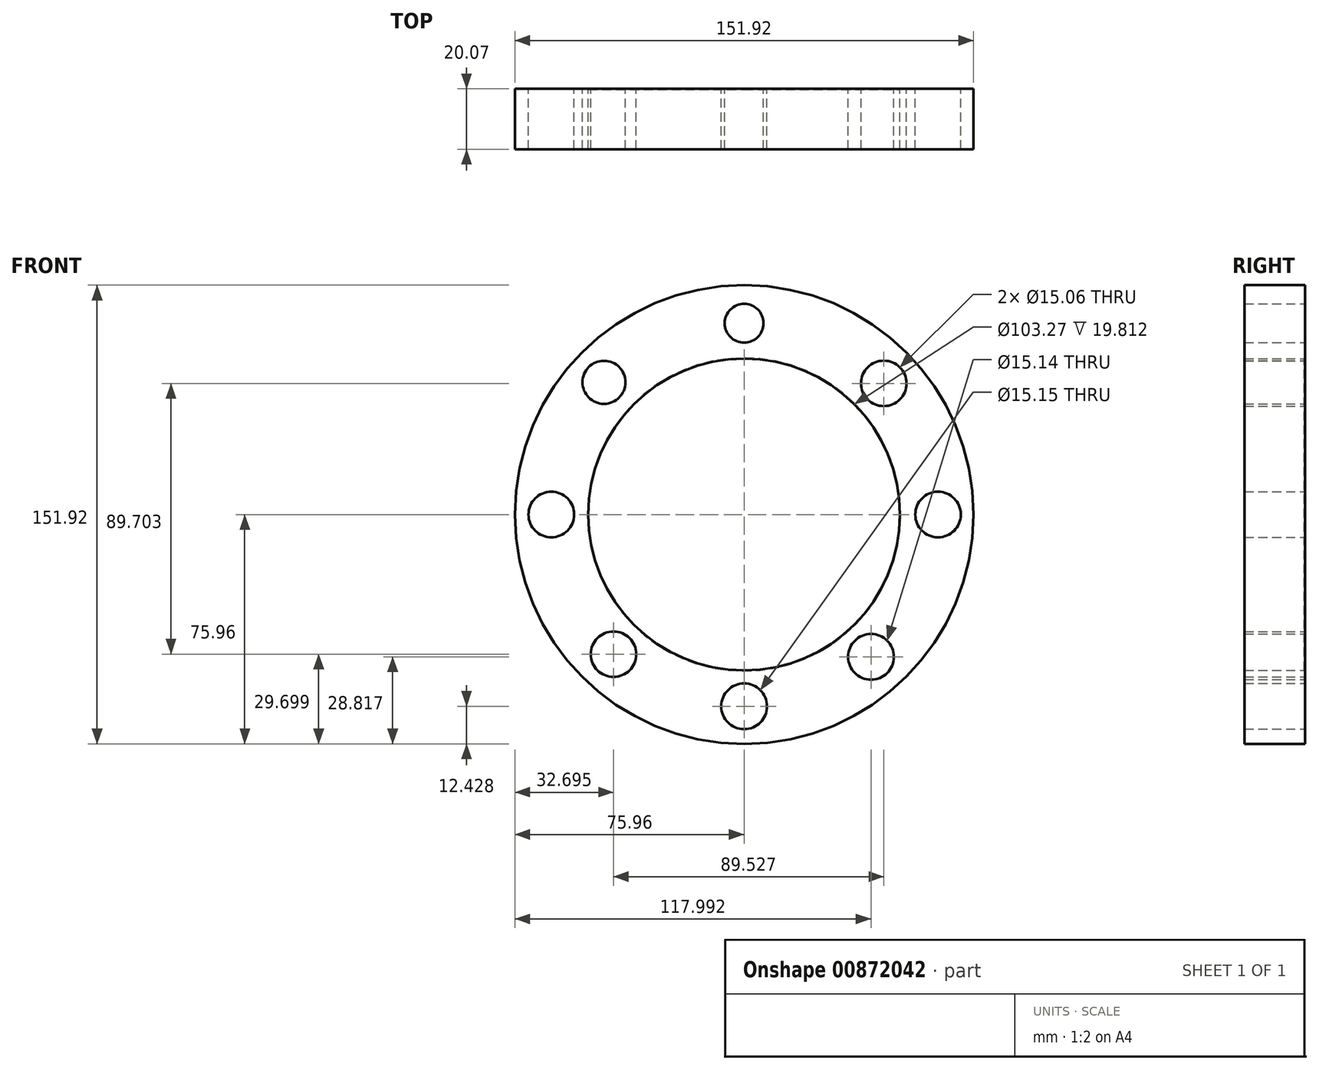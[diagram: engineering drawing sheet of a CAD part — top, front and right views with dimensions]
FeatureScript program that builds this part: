
annotation { "Feature Type Name" : "Feature", "Feature Type Description" : "" }
export const myFeature = defineFeature(function(context is Context, id is Id, definition is map)
    precondition{}
    {
        {
            var Q0;
            Q0=qCreatedBy(makeId("Front.planeOp"),FACE);
            var sketch = newSketch(context, id + "F0", { "sketchPlane" : qUnion([Q0])});
            skCircle(sketch, "E0", {"center": v(0, 0) * mm, "radius": 75.96 * mm});
            skCircle(sketch, "E1", {"center": v(0, 0) * mm, "radius": 51.63 * mm});
            skCircle(sketch, "E2", {"center": v(0, 0) * mm, "radius": 10.97 * mm});
            skCircle(sketch, "E3.cCircle", {"center": v(0, 0) * mm, "radius": 4.78 * mm, "construction": true});
            skLineSegment(sketch, "E3.0", {"start": v(2.76, -4.78) * mm, "end": v(-2.76, -4.78) * mm});
            skLineSegment(sketch, "E3.1", {"start": v(-2.76, -4.78) * mm, "end": v(-5.52, 0) * mm});
            skLineSegment(sketch, "E3.2", {"start": v(-5.52, 0) * mm, "end": v(-2.76, 4.78) * mm});
            skLineSegment(sketch, "E3.3", {"start": v(-2.76, 4.78) * mm, "end": v(2.76, 4.78) * mm});
            skLineSegment(sketch, "E3.4", {"start": v(2.76, 4.78) * mm, "end": v(5.52, 0) * mm});
            skLineSegment(sketch, "E3.5", {"start": v(5.52, 0) * mm, "end": v(2.76, -4.78) * mm});
            skPoint(sketch, "E3.0.midPoint", {"position": v(0, -4.78) * mm});
            skCircle(sketch, "E4", {"center": v(0, 0) * mm, "radius": 8.1 * mm});
            skLineSegment(sketch, "E5", {"start": v(0, 10.97) * mm, "end": v(5.52, 51.34) * mm});
            skLineSegment(sketch, "E6", {"start": v(0, -10.97) * mm, "end": v(-5.68, -51.32) * mm});
            skLineSegment(sketch, "E7", {"start": v(10.97, 0) * mm, "end": v(51.17, -6.89) * mm});
            skLineSegment(sketch, "E8", {"start": v(-10.97, 0) * mm, "end": v(-51.45, 4.34) * mm});
            skCircle(sketch, "E9", {"center": v(0, 0) * mm, "radius": 59.91 * mm});
            skLineSegment(sketch, "E10", {"start": v(10.83, -1.77) * mm, "end": v(51.63, 0) * mm});
            skLineSegment(sketch, "E11", {"start": v(2.48, 10.68) * mm, "end": v(0, 51.63) * mm});
            skLineSegment(sketch, "E12", {"start": v(-2.93, -10.57) * mm, "end": v(0, -51.63) * mm});
            skLineSegment(sketch, "E13", {"start": v(-10.5, 3.2) * mm, "end": v(-51.63, 0) * mm});
            skLineSegment(sketch, "E14", {"start": v(-6.47, 8.86) * mm, "end": v(-35.56, 37.44) * mm});
            skLineSegment(sketch, "E15", {"start": v(8.66, 6.73) * mm, "end": v(39, 33.83) * mm});
            skLineSegment(sketch, "E16", {"start": v(7.31, -10.97) * mm, "end": v(34.9, -38.06) * mm});
            skLineSegment(sketch, "E17", {"start": v(-8.55, -6.88) * mm, "end": v(-37.08, -35.93) * mm});
            skLineSegment(sketch, "E18", {"start": v(7.31, -8.17) * mm, "end": v(31.14, -41.18) * mm});
            skLineSegment(sketch, "E19", {"start": v(10.83, 4.85) * mm, "end": v(35.56, 37.44) * mm});
            skLineSegment(sketch, "E20", {"start": v(35.56, 37.44) * mm, "end": v(35.86, 36.22) * mm});
            skLineSegment(sketch, "E21", {"start": v(-8.7, 6.68) * mm, "end": v(-31.17, 41.16) * mm});
            skLineSegment(sketch, "E22", {"start": v(-6.47, -8.86) * mm, "end": v(-41.12, -31.23) * mm});
            skLineSegment(sketch, "E23", {"start": v(-41.12, -31.23) * mm, "end": v(-40.27, -30.58) * mm});
            skLineSegment(sketch, "E24", {"start": v(7.31, -10.97) * mm, "end": v(5.7, -9.38) * mm});
            skLineSegment(sketch, "E25", {"start": v(4.33, 10.08) * mm, "end": v(24.24, 45.59) * mm});
            skLineSegment(sketch, "E26", {"start": v(6.85, 8.57) * mm, "end": v(18.48, 48.21) * mm});
            skLineSegment(sketch, "E27", {"start": v(-2.48, 10.68) * mm, "end": v(-20.03, 47.59) * mm});
            skLineSegment(sketch, "E28", {"start": v(-20.03, 47.59) * mm, "end": v(-19.67, 46.71) * mm});
            skLineSegment(sketch, "E29", {"start": v(-5.27, 9.62) * mm, "end": v(-13.17, 49.92) * mm});
            skLineSegment(sketch, "E30", {"start": v(3.9, -10.25) * mm, "end": v(11.74, -50.28) * mm});
            skLineSegment(sketch, "E31", {"start": v(11.74, -50.28) * mm, "end": v(12.56, -49.68) * mm});
            skLineSegment(sketch, "E32", {"start": v(1.6, -10.85) * mm, "end": v(17.42, -48.6) * mm});
            skLineSegment(sketch, "E33", {"start": v(-4.02, -10.2) * mm, "end": v(-26, -44.61) * mm});
            skLineSegment(sketch, "E34", {"start": v(-5.22, -9.65) * mm, "end": v(-19.57, -47.78) * mm});
            skLineSegment(sketch, "E35", {"start": v(8.98, -6.3) * mm, "end": v(48.66, -17.28) * mm});
            skLineSegment(sketch, "E36", {"start": v(10.37, -3.58) * mm, "end": v(45.62, -24.18) * mm});
            skLineSegment(sketch, "E37", {"start": v(45.62, -24.18) * mm, "end": v(44.79, -23.75) * mm});
            skLineSegment(sketch, "E38", {"start": v(-10.97, -1.77) * mm, "end": v(-47.52, -20.2) * mm});
            skLineSegment(sketch, "E39", {"start": v(-47.52, -20.2) * mm, "end": v(-46.61, -19.83) * mm});
            skLineSegment(sketch, "E40", {"start": v(-9.55, -5.4) * mm, "end": v(-50.02, -12.8) * mm});
            skLineSegment(sketch, "E41", {"start": v(-9.6, 5.3) * mm, "end": v(-49.09, 16.01) * mm});
            skLineSegment(sketch, "E42", {"start": v(-9.6, 5.3) * mm, "end": v(-10.5, 3.2) * mm});
            skLineSegment(sketch, "E43", {"start": v(-10.5, 4.25) * mm, "end": v(-44.44, 26.3) * mm});
            skPoint(sketch, "E43.startSnap0", {"position": v(-10.05, 4.25) * mm});
            skLineSegment(sketch, "E44", {"start": v(10.77, 2.1) * mm, "end": v(46.11, 23.23) * mm});
            skLineSegment(sketch, "E45", {"start": v(10.83, 4.85) * mm, "end": v(49.36, 15.15) * mm});
            skSolve(sketch);
        }
        {
            var Q0;
            Q0=makeQuery(id+"F0.imprint","IMPRINT",FACE,{"disambiguationData":[TD([[makeQuery(id+"F0.imprint","IMPRINT",EDGE,{"derivedFrom":sQuery(id+"F0.wireOp",EDGE,"E0")}),1.0]])]});
            var Q1;
            Q1=makeQuery(id+"F0.imprint","IMPRINT",FACE,{"disambiguationData":[TD([[makeQuery(id+"F0.imprint","IMPRINT",EDGE,{"derivedFrom":sQuery(id+"F0.wireOp",EDGE,"E9")}),1.0]])]});
            extrude(context, id + "F1", {"entities" : qUnion([Q0, Q1]), "depth" : 20.07 * mm, "offsetDistance" : 25.4 * mm});
        }
        {
            var Q0;
            Q0=qCreatedBy(makeId("Front.planeOp"),FACE);
            var sketch = newSketch(context, id + "F2", { "sketchPlane" : qUnion([Q0])});
            skCircle(sketch, "E46", {"center": v(0, 63.36) * mm, "radius": 6.43 * mm});
            skCircle(sketch, "E47", {"center": v(0, -63.53) * mm, "radius": 7.58 * mm});
            skCircle(sketch, "E48", {"center": v(-63.88, 0) * mm, "radius": 7.55 * mm});
            skCircle(sketch, "E49", {"center": v(64.24, 0) * mm, "radius": 7.54 * mm});
            skCircle(sketch, "E50", {"center": v(46.26, 43.44) * mm, "radius": 7.53 * mm});
            skCircle(sketch, "E51", {"center": v(-46.44, 43.8) * mm, "radius": 7.13 * mm});
            skCircle(sketch, "E52", {"center": v(42.03, -47.14) * mm, "radius": 7.57 * mm});
            skCircle(sketch, "E53", {"center": v(-43.27, -46.26) * mm, "radius": 7.53 * mm});
            skSolve(sketch);
        }
        {
            var Q0;
            Q0=makeQuery(id+"F2.imprint","IMPRINT",FACE,{"disambiguationData":[TD([[makeQuery(id+"F2.imprint","IMPRINT",EDGE,{"derivedFrom":sQuery(id+"F2.wireOp",EDGE,"E49")}),1.0]])]});
            var Q1;
            Q1=makeQuery(id+"F2.imprint","IMPRINT",FACE,{"disambiguationData":[TD([[makeQuery(id+"F2.imprint","IMPRINT",EDGE,{"derivedFrom":sQuery(id+"F2.wireOp",EDGE,"E50")}),1.0]])]});
            var Q2;
            Q2=makeQuery(id+"F2.imprint","IMPRINT",FACE,{"disambiguationData":[TD([[makeQuery(id+"F2.imprint","IMPRINT",EDGE,{"derivedFrom":sQuery(id+"F2.wireOp",EDGE,"E46")}),1.0]])]});
            var Q3;
            Q3=makeQuery(id+"F2.imprint","IMPRINT",FACE,{"disambiguationData":[TD([[makeQuery(id+"F2.imprint","IMPRINT",EDGE,{"derivedFrom":sQuery(id+"F2.wireOp",EDGE,"E51")}),1.0]])]});
            var Q4;
            Q4=makeQuery(id+"F2.imprint","IMPRINT",FACE,{"disambiguationData":[TD([[makeQuery(id+"F2.imprint","IMPRINT",EDGE,{"derivedFrom":sQuery(id+"F2.wireOp",EDGE,"E48")}),1.0]])]});
            var Q5;
            Q5=makeQuery(id+"F2.imprint","IMPRINT",FACE,{"disambiguationData":[TD([[makeQuery(id+"F2.imprint","IMPRINT",EDGE,{"derivedFrom":sQuery(id+"F2.wireOp",EDGE,"E53")}),1.0]])]});
            var Q6;
            Q6=makeQuery(id+"F2.imprint","IMPRINT",FACE,{"disambiguationData":[TD([[makeQuery(id+"F2.imprint","IMPRINT",EDGE,{"derivedFrom":sQuery(id+"F2.wireOp",EDGE,"E47")}),1.0]])]});
            var Q7;
            Q7=makeQuery(id+"F2.imprint","IMPRINT",FACE,{"disambiguationData":[TD([[makeQuery(id+"F2.imprint","IMPRINT",EDGE,{"derivedFrom":sQuery(id+"F2.wireOp",EDGE,"E52")}),1.0]])]});
            extrude(context, id + "F3", {"entities" : qUnion([Q0, Q1, Q2, Q3, Q4, Q5, Q6, Q7]), "operationType" : NewBodyOperationType.REMOVE, "endBound" : BoundingType.THROUGH_ALL, "depth" : 25.4 * mm, "offsetDistance" : 25.4 * mm});
        }
        {
            var Q0;
            Q0=makeQuery(id+"F1.opExtrude","CAP_EDGE",EDGE,{"disambiguationData":[OSD([sQuery(id+"F0.wireOp",EDGE,"E1")])],"isStart":true});
            chamfer(context, id + "F4", {"entities" : qUnion([Q0]), "width" : 0.25 * mm, "tangentPropagation" : true});
        }
    });
